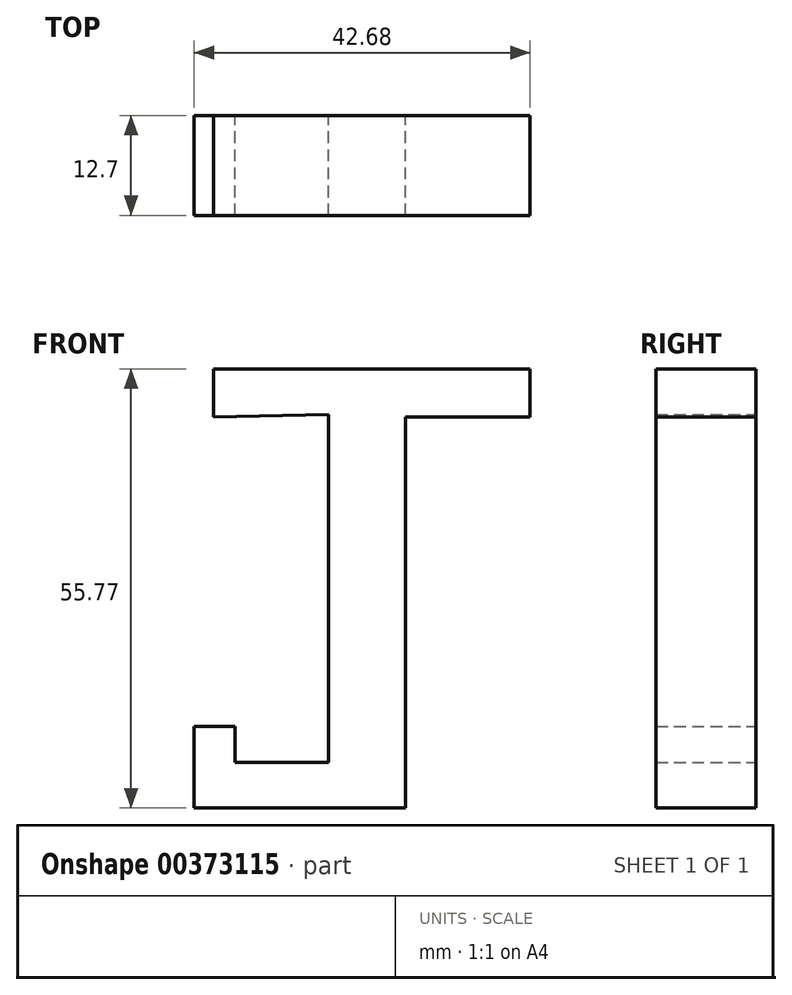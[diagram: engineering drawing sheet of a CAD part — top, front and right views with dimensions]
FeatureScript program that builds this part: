
annotation { "Feature Type Name" : "Feature", "Feature Type Description" : "" }
export const myFeature = defineFeature(function(context is Context, id is Id, definition is map)
    precondition{}
    {
        {
            var Q0;
            Q0=qCreatedBy(makeId("Front.planeOp"),FACE);
            var sketch = newSketch(context, id + "F0", { "sketchPlane" : qUnion([Q0])});
            skLineSegment(sketch, "E0", {"start": v(26.2, 30.63) * mm, "end": v(26.2, -13.56) * mm});
            skLineSegment(sketch, "E1", {"start": v(26.2, -13.56) * mm, "end": v(14.33, -13.56) * mm});
            skLineSegment(sketch, "E2", {"start": v(14.33, -13.56) * mm, "end": v(14.33, -9) * mm});
            skLineSegment(sketch, "E3", {"start": v(14.33, -9) * mm, "end": v(9.14, -9) * mm});
            skLineSegment(sketch, "E4", {"start": v(9.14, -9) * mm, "end": v(9.14, -19.35) * mm});
            skLineSegment(sketch, "E5", {"start": v(9.14, -19.35) * mm, "end": v(35.97, -19.35) * mm});
            skLineSegment(sketch, "E6", {"start": v(35.97, -19.35) * mm, "end": v(35.97, 30.33) * mm});
            skLineSegment(sketch, "E7", {"start": v(35.97, 30.33) * mm, "end": v(51.82, 30.33) * mm});
            skLineSegment(sketch, "E8", {"start": v(51.82, 30.33) * mm, "end": v(51.82, 36.42) * mm});
            skLineSegment(sketch, "E9", {"start": v(51.82, 36.42) * mm, "end": v(11.58, 36.42) * mm});
            skLineSegment(sketch, "E10", {"start": v(11.58, 36.42) * mm, "end": v(11.58, 30.33) * mm});
            skLineSegment(sketch, "E11", {"start": v(11.58, 30.33) * mm, "end": v(26.2, 30.63) * mm});
            skSolve(sketch);
        }
        {
            var Q0;
            Q0 = qSketchRegion(id + "F0", true);
            extrude(context, id + "F1", {"entities" : qUnion([Q0]), "depth" : 12.7 * mm});
        }
    });
